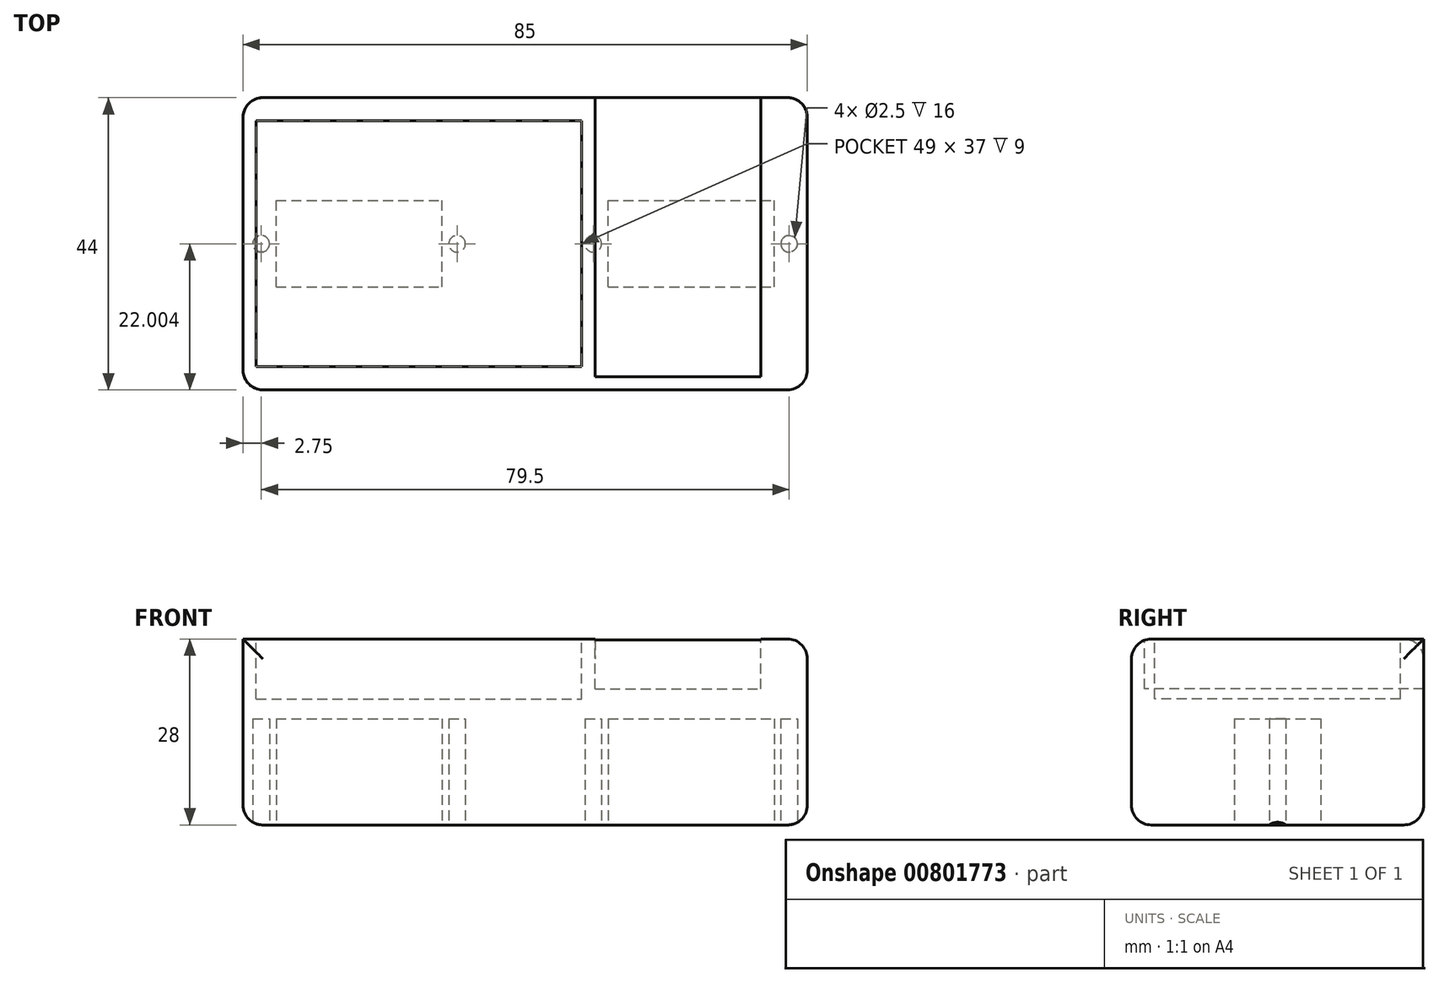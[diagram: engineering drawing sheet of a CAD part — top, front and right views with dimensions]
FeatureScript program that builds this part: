
annotation { "Feature Type Name" : "Feature", "Feature Type Description" : "" }
export const myFeature = defineFeature(function(context is Context, id is Id, definition is map)
    precondition{}
    {
        {
            var Q0;
            Q0=qCreatedBy(makeId("Top.planeOp"),FACE);
            var sketch = newSketch(context, id + "F0", { "sketchPlane" : qUnion([Q0])});
            skLineSegment(sketch, "E0.bottom", {"start": v(-29.75, 12.76) * mm, "end": v(55.25, 12.76) * mm});
            skLineSegment(sketch, "E0.top", {"start": v(-29.75, -31.24) * mm, "end": v(55.25, -31.24) * mm});
            skLineSegment(sketch, "E0.left", {"start": v(-29.75, 12.76) * mm, "end": v(-29.75, -31.24) * mm});
            skLineSegment(sketch, "E0.right", {"start": v(55.25, 12.76) * mm, "end": v(55.25, -31.24) * mm});
            skSolve(sketch);
        }
        {
            var Q0;
            Q0 = qSketchRegion(id + "F0", true);
            extrude(context, id + "F1", {"entities" : qUnion([Q0]), "depth" : 28 * mm, "offsetDistance" : 25 * mm});
        }
        {
            var Q0;
            Q0=makeQuery(id+"F1.opExtrude","CAP_FACE",FACE,{"disambiguationData":[OSD([sQuery(id+"F0.wireOp",EDGE,"E0.bottom"),sQuery(id+"F0.wireOp",EDGE,"E0.top"),sQuery(id+"F0.wireOp",EDGE,"E0.left"),sQuery(id+"F0.wireOp",EDGE,"E0.right")])],"isStart":false});
            var sketch = newSketch(context, id + "F2", { "sketchPlane" : qUnion([Q0])});
            skLineSegment(sketch, "E1.bottom", {"start": v(-27.75, 9.26) * mm, "end": v(21.25, 9.26) * mm});
            skLineSegment(sketch, "E1.top", {"start": v(-27.75, -27.74) * mm, "end": v(21.25, -27.74) * mm});
            skLineSegment(sketch, "E1.left", {"start": v(-27.75, 9.26) * mm, "end": v(-27.75, -27.74) * mm});
            skLineSegment(sketch, "E1.right", {"start": v(21.25, 9.26) * mm, "end": v(21.25, -27.74) * mm});
            skLineSegment(sketch, "E2.bottom", {"start": v(23.25, 12.76) * mm, "end": v(48.25, 12.76) * mm});
            skLineSegment(sketch, "E2.top", {"start": v(23.25, -29.24) * mm, "end": v(48.25, -29.24) * mm});
            skLineSegment(sketch, "E2.left", {"start": v(23.25, 12.76) * mm, "end": v(23.25, -29.24) * mm});
            skLineSegment(sketch, "E2.right", {"start": v(48.25, 12.76) * mm, "end": v(48.25, -29.24) * mm});
            skSolve(sketch);
        }
        {
            var Q0;
            Q0=makeQuery(id+"F2.imprint","IMPRINT",FACE,{"disambiguationData":[TD([[makeQuery(id+"F2.imprint","IMPRINT",EDGE,{"derivedFrom":sQuery(id+"F2.wireOp",EDGE,"E1.bottom")}),-1.0]])]});
            extrude(context, id + "F3", {"entities" : qUnion([Q0]), "operationType" : NewBodyOperationType.REMOVE, "oppositeDirection" : true, "depth" : 9 * mm, "offsetDistance" : 25 * mm});
        }
        {
            var Q0;
            Q0=makeQuery(id+"F2.imprint","IMPRINT",FACE,{"disambiguationData":[TD([[makeQuery(id+"F2.imprint","IMPRINT",EDGE,{"derivedFrom":sQuery(id+"F2.wireOp",EDGE,"E2.bottom")}),-1.0]])]});
            extrude(context, id + "F4", {"entities" : qUnion([Q0]), "operationType" : NewBodyOperationType.REMOVE, "oppositeDirection" : true, "depth" : 7.5 * mm, "offsetDistance" : 25 * mm});
        }
        {
            var Q0;
            Q0=makeQuery(id+"F1.opExtrude","CAP_FACE",FACE,{"disambiguationData":[OSD([sQuery(id+"F0.wireOp",EDGE,"E0.bottom"),sQuery(id+"F0.wireOp",EDGE,"E0.top"),sQuery(id+"F0.wireOp",EDGE,"E0.left"),sQuery(id+"F0.wireOp",EDGE,"E0.right")])],"isStart":true});
            var sketch = newSketch(context, id + "F5", { "sketchPlane" : qUnion([Q0])});
            skLineSegment(sketch, "E3.bottom", {"start": v(-24.75, 15.74) * mm, "end": v(0.25, 15.74) * mm});
            skLineSegment(sketch, "E3.top", {"start": v(-24.75, 2.74) * mm, "end": v(0.25, 2.74) * mm});
            skLineSegment(sketch, "E3.left", {"start": v(-24.75, 15.74) * mm, "end": v(-24.75, 2.74) * mm});
            skLineSegment(sketch, "E3.right", {"start": v(0.25, 15.74) * mm, "end": v(0.25, 2.74) * mm});
            skLineSegment(sketch, "E4.bottom", {"start": v(25.25, 15.74) * mm, "end": v(50.25, 15.74) * mm});
            skLineSegment(sketch, "E4.top", {"start": v(25.25, 2.74) * mm, "end": v(50.25, 2.74) * mm});
            skLineSegment(sketch, "E4.left", {"start": v(25.25, 15.74) * mm, "end": v(25.25, 2.74) * mm});
            skLineSegment(sketch, "E4.right", {"start": v(50.25, 15.74) * mm, "end": v(50.25, 2.74) * mm});
            skCircle(sketch, "E5", {"center": v(-27, 9.24) * mm, "radius": 1.25 * mm});
            skCircle(sketch, "E6", {"center": v(2.5, 9.24) * mm, "radius": 1.25 * mm});
            skCircle(sketch, "E7", {"center": v(23, 9.24) * mm, "radius": 1.25 * mm});
            skCircle(sketch, "E8", {"center": v(52.5, 9.24) * mm, "radius": 1.25 * mm});
            skSolve(sketch);
        }
        {
            var Q0;
            Q0 = qSketchRegion(id + "F5", true);
            extrude(context, id + "F6", {"entities" : qUnion([Q0]), "operationType" : NewBodyOperationType.REMOVE, "oppositeDirection" : true, "depth" : 16 * mm, "offsetDistance" : 25 * mm});
        }
        {
            var Q0;
            Q0=makeQuery(id+"F1.opExtrude","SWEPT_EDGE",EDGE,{"disambiguationData":[OSD([sQuery(id+"F0.wireOp",EDGE,"E0.top"),sQuery(id+"F0.wireOp",EDGE,"E0.right")])]});
            var Q1;
            Q1=makeQuery(id+"F1.opExtrude","SWEPT_EDGE",EDGE,{"disambiguationData":[OSD([sQuery(id+"F0.wireOp",EDGE,"E0.bottom"),sQuery(id+"F0.wireOp",EDGE,"E0.right")])]});
            var Q2;
            Q2=makeQuery(id+"F1.opExtrude","SWEPT_EDGE",EDGE,{"disambiguationData":[OSD([sQuery(id+"F0.wireOp",EDGE,"E0.top"),sQuery(id+"F0.wireOp",EDGE,"E0.left")])]});
            var Q3;
            Q3=makeQuery(id+"F1.opExtrude","SWEPT_EDGE",EDGE,{"disambiguationData":[OSD([sQuery(id+"F0.wireOp",EDGE,"E0.bottom"),sQuery(id+"F0.wireOp",EDGE,"E0.left")])]});
            var Q4;
            Q4=makeQuery(id+"F1.opExtrude","CAP_EDGE",EDGE,{"disambiguationData":[OSD([sQuery(id+"F0.wireOp",EDGE,"E0.bottom")])],"isStart":true});
            var Q5;
            Q5=makeQuery(id+"F1.opExtrude","CAP_EDGE",EDGE,{"disambiguationData":[OSD([sQuery(id+"F0.wireOp",EDGE,"E0.left")])],"isStart":true});
            var Q6;
            Q6=makeQuery(id+"F1.opExtrude","CAP_EDGE",EDGE,{"disambiguationData":[OSD([sQuery(id+"F0.wireOp",EDGE,"E0.right")])],"isStart":true});
            var Q7;
            Q7=makeQuery(id+"F1.opExtrude","CAP_EDGE",EDGE,{"disambiguationData":[OSD([sQuery(id+"F0.wireOp",EDGE,"E0.top")])],"isStart":true});
            var Q8;
            {var subQ0=sQuery(id+"F0.wireOp",EDGE,"E0.bottom");var subQ1=sQuery(id+"F0.wireOp",EDGE,"E0.left");Q8=makeQuery(id+"F4.boolean.opBoolean","SPLIT",EDGE,{"disambiguationData":[TD([makeQuery(id+"F1.opExtrude","SWEPT_FACE",FACE,{"disambiguationData":[OSD([subQ1])]})])],"derivedFrom":makeQuery(id+"F1.opExtrude","CAP_EDGE",EDGE,{"disambiguationData":[OSD([subQ0])],"isStart":false})});}
            var Q9;
            Q9=makeQuery(id+"F1.opExtrude","CAP_EDGE",EDGE,{"disambiguationData":[OSD([sQuery(id+"F0.wireOp",EDGE,"E0.top")])],"isStart":false});
            var Q10;
            Q10=makeQuery(id+"F1.opExtrude","CAP_EDGE",EDGE,{"disambiguationData":[OSD([sQuery(id+"F0.wireOp",EDGE,"E0.right")])],"isStart":false});
            fillet(context, id + "F7", {"entities" : qUnion([Q0, Q1, Q2, Q3, Q4, Q5, Q6, Q7, Q8, Q9, Q10]), "radius" : 3 * mm, "tangentPropagation" : true, "allowEdgeOverflow" : false});
        }
    });
